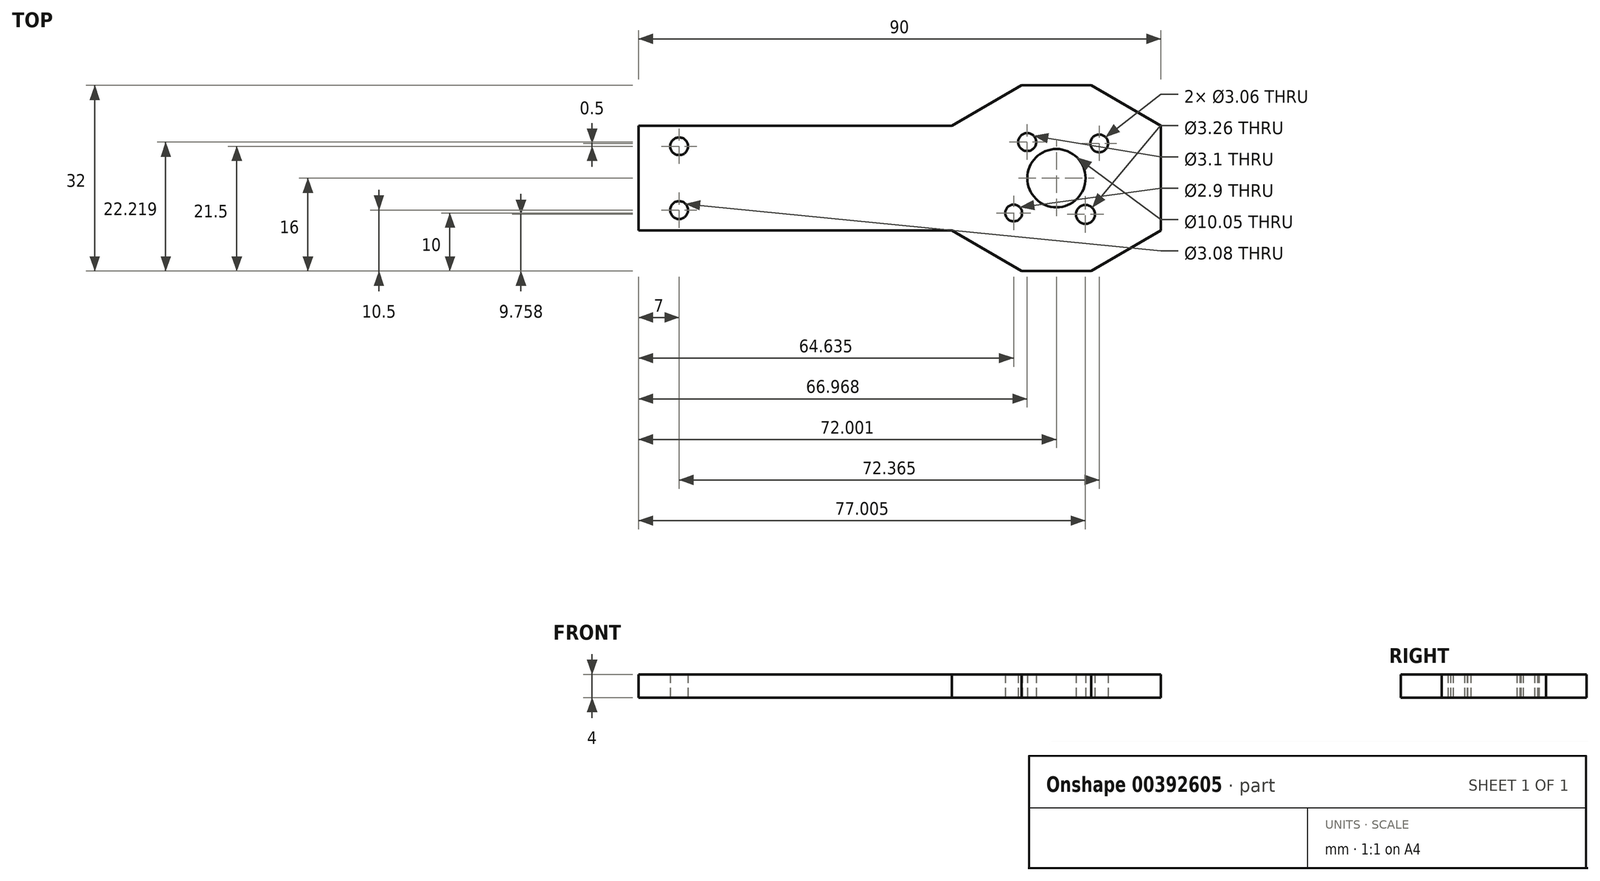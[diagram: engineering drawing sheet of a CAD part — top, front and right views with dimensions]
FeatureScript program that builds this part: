
annotation { "Feature Type Name" : "Feature", "Feature Type Description" : "" }
export const myFeature = defineFeature(function(context is Context, id is Id, definition is map)
    precondition{}
    {
        {
            var Q0;
            Q0=qCreatedBy(makeId("Top.planeOp"),FACE);
            var sketch = newSketch(context, id + "F0", { "sketchPlane" : qUnion([Q0])});
            skLineSegment(sketch, "E0", {"start": v(-35.5, 18) * mm, "end": v(18.5, 18) * mm});
            skLineSegment(sketch, "E1", {"start": v(-35.5, 18) * mm, "end": v(-35.5, 0) * mm});
            skLineSegment(sketch, "E2", {"start": v(-35.5, 0) * mm, "end": v(18.5, 0) * mm});
            skLineSegment(sketch, "E3", {"start": v(18.5, 0) * mm, "end": v(30.5, -7) * mm});
            skLineSegment(sketch, "E4", {"start": v(30.5, -7) * mm, "end": v(42.5, -7) * mm});
            skLineSegment(sketch, "E5", {"start": v(42.5, -7) * mm, "end": v(54.5, 0) * mm});
            skLineSegment(sketch, "E6", {"start": v(54.5, 0) * mm, "end": v(54.5, 18) * mm});
            skLineSegment(sketch, "E7", {"start": v(54.5, 18) * mm, "end": v(42.5, 25) * mm});
            skLineSegment(sketch, "E8", {"start": v(42.5, 25) * mm, "end": v(30.5, 25) * mm});
            skLineSegment(sketch, "E9", {"start": v(30.5, 25) * mm, "end": v(18.5, 18) * mm});
            skCircle(sketch, "E10", {"center": v(36.5, 9) * mm, "radius": 5.02 * mm});
            skCircle(sketch, "E11", {"center": v(29.14, 3) * mm, "radius": 1.45 * mm});
            skCircle(sketch, "E12", {"center": v(43.87, 15) * mm, "radius": 1.53 * mm});
            skCircle(sketch, "E13", {"center": v(31.47, 15.22) * mm, "radius": 1.55 * mm});
            skCircle(sketch, "E14", {"center": v(41.5, 2.76) * mm, "radius": 1.63 * mm});
            skCircle(sketch, "E15", {"center": v(-28.5, 14.5) * mm, "radius": 1.53 * mm});
            skCircle(sketch, "E16", {"center": v(-28.5, 3.5) * mm, "radius": 1.54 * mm});
            skSolve(sketch);
        }
        {
            var Q0;
            Q0 = qSketchRegion(id + "F0", true);
            extrude(context, id + "F1", {"entities" : qUnion([Q0]), "depth" : 4 * mm});
        }
    });
